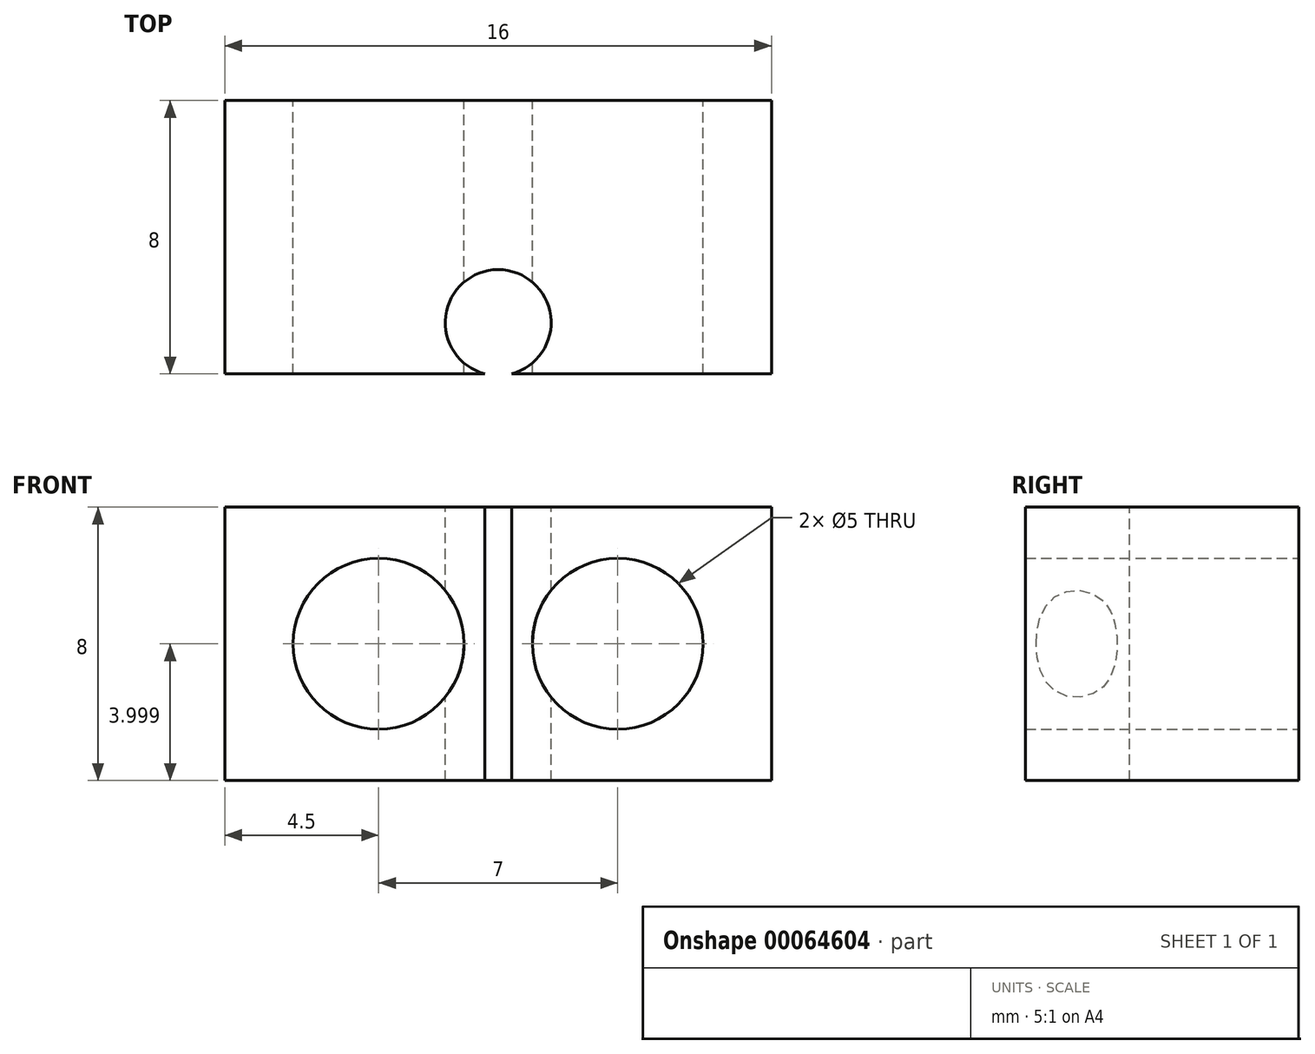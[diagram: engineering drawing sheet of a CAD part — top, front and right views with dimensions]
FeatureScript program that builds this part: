
annotation { "Feature Type Name" : "Feature", "Feature Type Description" : "" }
export const myFeature = defineFeature(function(context is Context, id is Id, definition is map)
    precondition{}
    {
        {
            var Q0;
            Q0=qCreatedBy(makeId("Front.planeOp"),FACE);
            var sketch = newSketch(context, id + "F0", { "sketchPlane" : qUnion([Q0])});
            skLineSegment(sketch, "E0.bottom", {"start": v(-3.96, 9.73) * mm, "end": v(12.04, 9.73) * mm});
            skLineSegment(sketch, "E0.top", {"start": v(-3.96, 1.73) * mm, "end": v(12.04, 1.73) * mm});
            skLineSegment(sketch, "E0.left", {"start": v(-3.96, 9.73) * mm, "end": v(-3.96, 1.73) * mm});
            skLineSegment(sketch, "E0.right", {"start": v(12.04, 9.73) * mm, "end": v(12.04, 1.73) * mm});
            skCircle(sketch, "E1", {"center": v(0.54, 5.73) * mm, "radius": 2.5 * mm});
            skCircle(sketch, "E2", {"center": v(7.54, 5.73) * mm, "radius": 2.5 * mm});
            skLineSegment(sketch, "E3", {"start": v(4.04, 9.73) * mm, "end": v(4.04, 1.73) * mm, "construction": true});
            skSolve(sketch);
        }
        {
            var Q0;
            Q0=makeQuery(id+"F0.imprint","IMPRINT",FACE,{"disambiguationData":[TD([[makeQuery(id+"F0.imprint","IMPRINT",EDGE,{"derivedFrom":sQuery(id+"F0.wireOp",EDGE,"E0.bottom")}),-1.0]])]});
            extrude(context, id + "F1", {"entities" : qUnion([Q0]), "depth" : 8 * mm});
        }
        {
            var Q0;
            Q0=makeQuery(id+"F1.opExtrude","SWEPT_FACE",FACE,{"disambiguationData":[OSD([sQuery(id+"F0.wireOp",EDGE,"E0.bottom")])]});
            var sketch = newSketch(context, id + "F2", { "sketchPlane" : qUnion([Q0])});
            skCircle(sketch, "E4", {"center": v(4.04, -6.5) * mm, "radius": 1.55 * mm});
            skPoint(sketch, "E4.centerSnap0", {"position": v(4.04, -8) * mm});
            skSolve(sketch);
        }
        {
            var Q0;
            {var subQ0=sQuery(id+"F2.wireOp",EDGE,"E4");var subQ1=makeQuery(id+"F1.opExtrude","CAP_EDGE",EDGE,{"disambiguationData":[OSD([sQuery(id+"F0.wireOp",EDGE,"E0.bottom")])],"isStart":false});var subQ2=makeQuery(id+"F2.imprint","INTERSECT",VERTEX,{"disambiguationData":[OD(0.0)],"derivedFrom":[subQ1,subQ0]});Q0=makeQuery(id+"F2.imprint","IMPRINT",FACE,{"disambiguationData":[TD([[makeQuery(id+"F2.imprint","IMPRINT",EDGE,{"disambiguationData":[TD([[subQ2,1.0]])],"derivedFrom":subQ0}),1.0]])]});}
            extrude(context, id + "F3", {"entities" : qUnion([Q0]), "operationType" : NewBodyOperationType.REMOVE, "endBound" : BoundingType.THROUGH_ALL, "oppositeDirection" : true, "depth" : 25 * mm});
        }
    });
